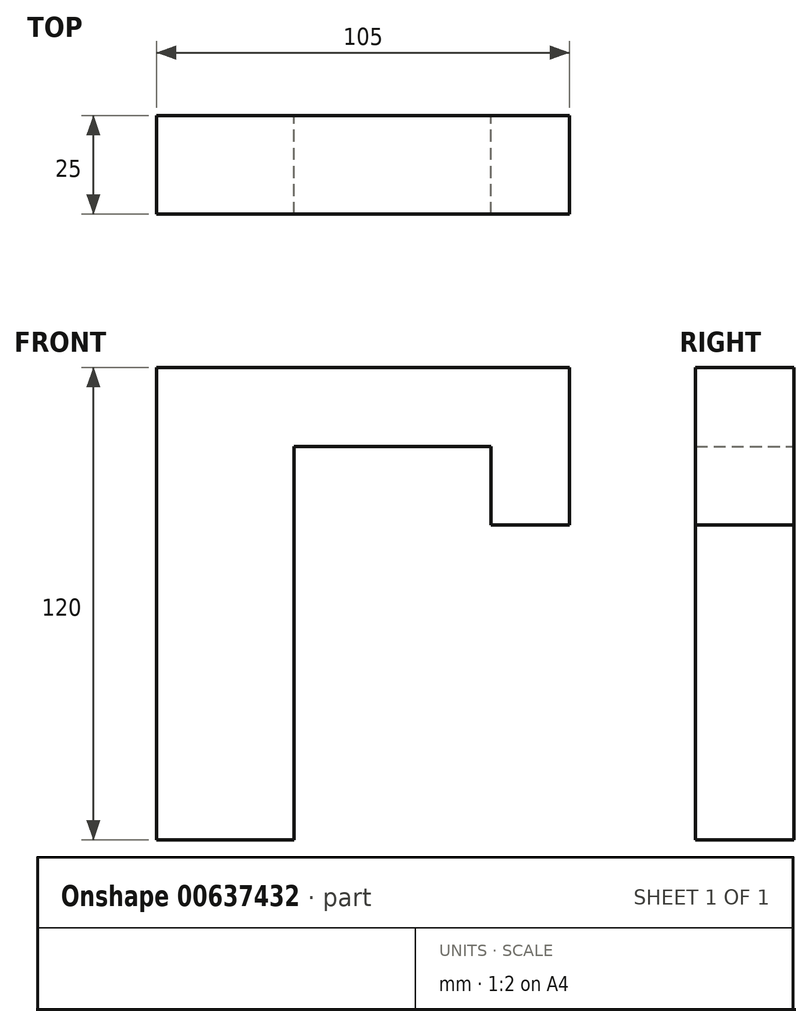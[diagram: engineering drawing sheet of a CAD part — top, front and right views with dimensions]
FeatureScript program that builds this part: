
annotation { "Feature Type Name" : "Feature", "Feature Type Description" : "" }
export const myFeature = defineFeature(function(context is Context, id is Id, definition is map)
    precondition{}
    {
        {
            var Q0;
            Q0=qCreatedBy(makeId("Front.planeOp"),FACE);
            var sketch = newSketch(context, id + "F0", { "sketchPlane" : qUnion([Q0])});
            skLineSegment(sketch, "E0", {"start": v(-115.87, 57.77) * mm, "end": v(-115.87, -62.23) * mm});
            skLineSegment(sketch, "E1", {"start": v(-115.87, -62.23) * mm, "end": v(-80.87, -62.23) * mm});
            skLineSegment(sketch, "E2", {"start": v(-80.87, -62.23) * mm, "end": v(-80.87, 37.77) * mm});
            skLineSegment(sketch, "E3", {"start": v(-80.87, 37.77) * mm, "end": v(-30.87, 37.77) * mm});
            skLineSegment(sketch, "E4", {"start": v(-30.87, 37.77) * mm, "end": v(-30.87, 17.77) * mm});
            skLineSegment(sketch, "E5", {"start": v(-30.87, 17.77) * mm, "end": v(-10.87, 17.77) * mm});
            skLineSegment(sketch, "E6", {"start": v(-10.87, 17.77) * mm, "end": v(-10.87, 57.77) * mm});
            skLineSegment(sketch, "E7", {"start": v(-10.87, 57.77) * mm, "end": v(-115.87, 57.77) * mm});
            skSolve(sketch);
        }
        {
            var Q0;
            Q0 = qSketchRegion(id + "F0", true);
            extrude(context, id + "F1", {"entities" : qUnion([Q0]), "depth" : 25 * mm, "offsetDistance" : 25 * mm});
        }
    });
